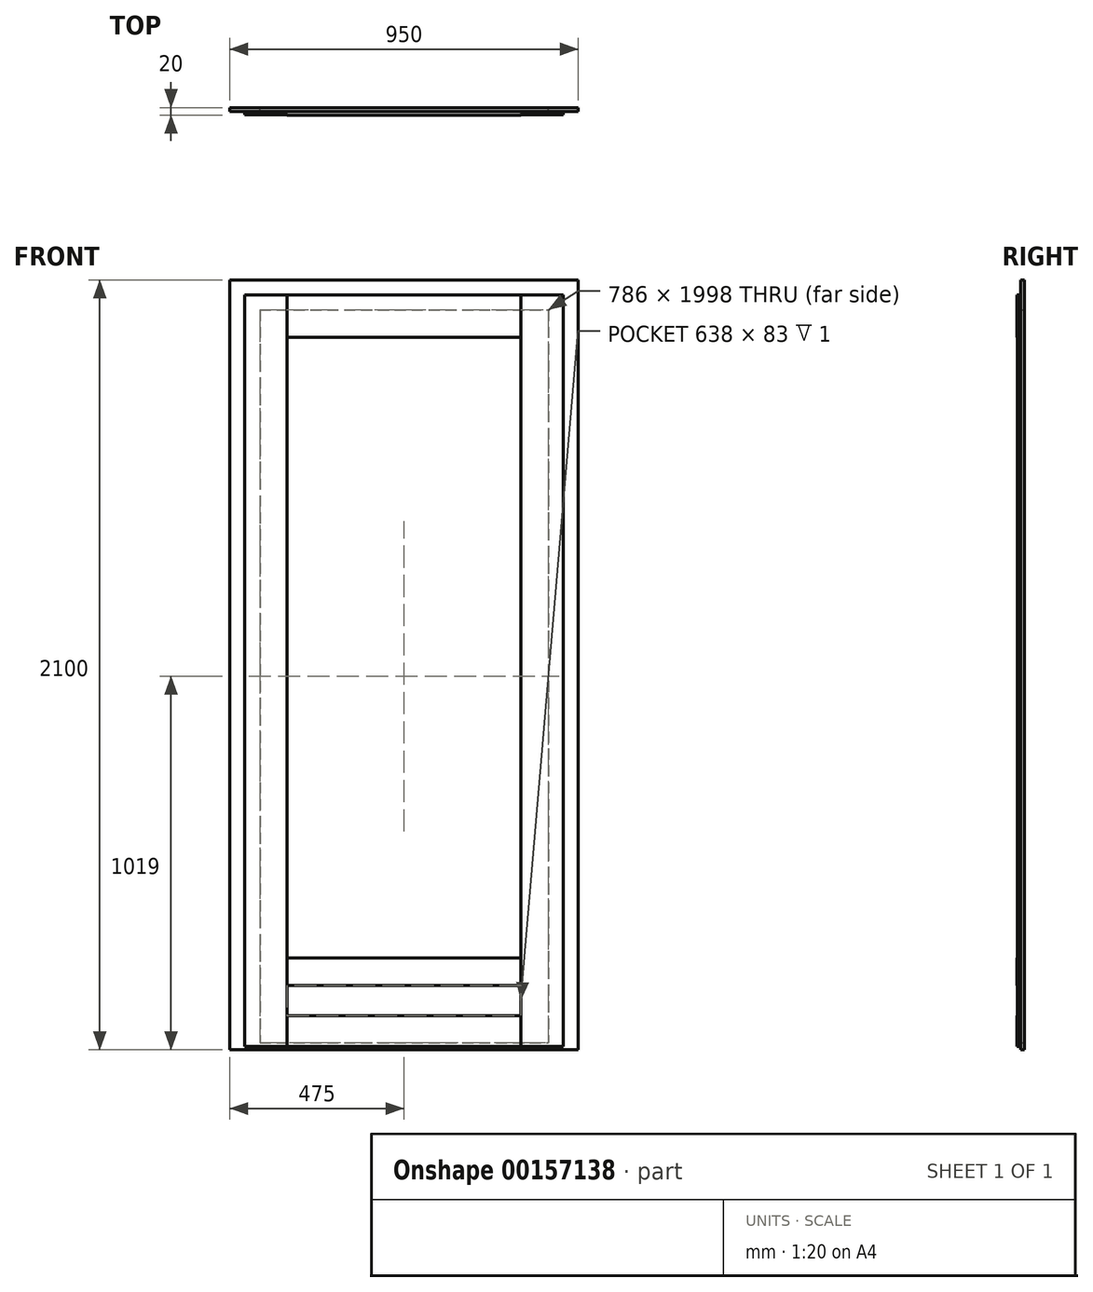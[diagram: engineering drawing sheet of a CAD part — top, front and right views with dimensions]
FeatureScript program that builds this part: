
annotation { "Feature Type Name" : "Feature", "Feature Type Description" : "" }
export const myFeature = defineFeature(function(context is Context, id is Id, definition is map)
    precondition{}
    {
        {
            var Q0;
            Q0=qCreatedBy(makeId("Front.planeOp"),FACE);
            var sketch = newSketch(context, id + "F0", { "sketchPlane" : qUnion([Q0])});
            skLineSegment(sketch, "E0.bottom", {"start": v(0, 0) * mm, "end": v(950, 0) * mm});
            skLineSegment(sketch, "E0.top", {"start": v(0, 2100) * mm, "end": v(950, 2100) * mm});
            skLineSegment(sketch, "E0.left", {"start": v(0, 0) * mm, "end": v(0, 2100) * mm});
            skLineSegment(sketch, "E0.right", {"start": v(950, 0) * mm, "end": v(950, 2100) * mm});
            skLineSegment(sketch, "E1.bottom", {"start": v(82, 2018) * mm, "end": v(868, 2018) * mm});
            skLineSegment(sketch, "E1.top", {"start": v(82, 20) * mm, "end": v(868, 20) * mm});
            skLineSegment(sketch, "E1.left", {"start": v(82, 2018) * mm, "end": v(82, 20) * mm});
            skLineSegment(sketch, "E1.right", {"start": v(868, 2018) * mm, "end": v(868, 20) * mm});
            skSolve(sketch);
        }
        {
            var Q0;
            Q0 = qSketchRegion(id + "F0", true);
            extrude(context, id + "F1", {"entities" : qUnion([Q0]), "depth" : 10 * mm});
        }
        {
            var Q0;
            Q0=makeQuery(id+"F1.opExtrude","CAP_FACE",FACE,{"disambiguationData":[OSD([sQuery(id+"F0.wireOp",EDGE,"E0.bottom"),sQuery(id+"F0.wireOp",EDGE,"E0.top"),sQuery(id+"F0.wireOp",EDGE,"E0.left"),sQuery(id+"F0.wireOp",EDGE,"E0.right"),sQuery(id+"F0.wireOp",EDGE,"E1.bottom"),sQuery(id+"F0.wireOp",EDGE,"E1.top"),sQuery(id+"F0.wireOp",EDGE,"E1.left"),sQuery(id+"F0.wireOp",EDGE,"E1.right")])],"isStart":false});
            var sketch = newSketch(context, id + "F2", { "sketchPlane" : qUnion([Q0])});
            skLineSegment(sketch, "E2.bottom", {"start": v(41, 2059) * mm, "end": v(909, 2059) * mm});
            skLineSegment(sketch, "E2.top", {"start": v(41, 10) * mm, "end": v(909, 10) * mm});
            skLineSegment(sketch, "E2.left", {"start": v(41, 2059) * mm, "end": v(41, 10) * mm});
            skLineSegment(sketch, "E2.right", {"start": v(909, 2059) * mm, "end": v(909, 10) * mm});
            skLineSegment(sketch, "E3.bottom", {"start": v(156, 1944) * mm, "end": v(794, 1944) * mm});
            skLineSegment(sketch, "E3.top", {"start": v(156, 251) * mm, "end": v(794, 251) * mm});
            skLineSegment(sketch, "E3.left", {"start": v(156, 1944) * mm, "end": v(156, 251) * mm});
            skLineSegment(sketch, "E3.right", {"start": v(794, 1944) * mm, "end": v(794, 251) * mm});
            skSolve(sketch);
        }
        {
            var Q0;
            Q0=makeQuery(id+"F2.imprint","IMPRINT",FACE,{"disambiguationData":[TD([[makeQuery(id+"F2.imprint","IMPRINT",EDGE,{"derivedFrom":sQuery(id+"F2.wireOp",EDGE,"E2.bottom")}),-1.0]])]});
            var Q1;
            Q1 = qSketchRegion(id + "F2", true);
            extrude(context, id + "F3", {"entities" : qUnion([Q0, Q1]), "depth" : 10 * mm});
        }
        {
            var Q0;
            Q0=makeQuery(id+"F3.opExtrude","CAP_FACE",FACE,{"disambiguationData":[OSD([sQuery(id+"F2.wireOp",EDGE,"E2.bottom"),sQuery(id+"F2.wireOp",EDGE,"E2.top"),sQuery(id+"F2.wireOp",EDGE,"E2.left"),sQuery(id+"F2.wireOp",EDGE,"E2.right"),sQuery(id+"F2.wireOp",EDGE,"E3.bottom"),sQuery(id+"F2.wireOp",EDGE,"E3.top"),sQuery(id+"F2.wireOp",EDGE,"E3.left"),sQuery(id+"F2.wireOp",EDGE,"E3.right")])],"isStart":false});
            var sketch = newSketch(context, id + "F4", { "sketchPlane" : qUnion([Q0])});
            skLineSegment(sketch, "E4.bottom", {"start": v(41, 2059) * mm, "end": v(156, 2059) * mm});
            skLineSegment(sketch, "E4.top", {"start": v(41, 10) * mm, "end": v(156, 10) * mm});
            skLineSegment(sketch, "E4.left", {"start": v(41, 2059) * mm, "end": v(41, 10) * mm});
            skLineSegment(sketch, "E4.right", {"start": v(156, 2059) * mm, "end": v(156, 10) * mm});
            skLineSegment(sketch, "E5.bottom", {"start": v(794, 2059) * mm, "end": v(909, 2059) * mm});
            skLineSegment(sketch, "E5.top", {"start": v(794, 10) * mm, "end": v(909, 10) * mm});
            skLineSegment(sketch, "E5.left", {"start": v(794, 2059) * mm, "end": v(794, 10) * mm});
            skLineSegment(sketch, "E5.right", {"start": v(909, 2059) * mm, "end": v(909, 10) * mm});
            skSolve(sketch);
        }
        {
            var Q0;
            Q0 = qSketchRegion(id + "F4", true);
            extrude(context, id + "F5", {"entities" : qUnion([Q0]), "operationType" : NewBodyOperationType.REMOVE, "oppositeDirection" : true, "depth" : 1 * mm});
        }
        {
            var Q0;
            {var subQ0=sQuery(id+"F2.wireOp",EDGE,"E2.top");var subQ1=sQuery(id+"F2.wireOp",EDGE,"E3.top");Q0=makeQuery(id+"F5.boolean.opBoolean","SPLIT",FACE,{"disambiguationData":[TD([makeQuery(id+"F3.opExtrude","SWEPT_FACE",FACE,{"disambiguationData":[OSD([subQ0])]})])],"derivedFrom":makeQuery(id+"F3.opExtrude","CAP_FACE",FACE,{"disambiguationData":[OSD([sQuery(id+"F2.wireOp",EDGE,"E2.bottom"),subQ0,sQuery(id+"F2.wireOp",EDGE,"E2.left"),sQuery(id+"F2.wireOp",EDGE,"E2.right"),sQuery(id+"F2.wireOp",EDGE,"E3.bottom"),subQ1,sQuery(id+"F2.wireOp",EDGE,"E3.left"),sQuery(id+"F2.wireOp",EDGE,"E3.right")])],"isStart":false})});}
            var sketch = newSketch(context, id + "F6", { "sketchPlane" : qUnion([Q0])});
            skLineSegment(sketch, "E6.bottom", {"start": v(156, 176) * mm, "end": v(794, 176) * mm});
            skLineSegment(sketch, "E6.top", {"start": v(156, 93) * mm, "end": v(794, 93) * mm});
            skLineSegment(sketch, "E6.left", {"start": v(156, 176) * mm, "end": v(156, 93) * mm});
            skLineSegment(sketch, "E6.right", {"start": v(794, 176) * mm, "end": v(794, 93) * mm});
            skSolve(sketch);
        }
        {
            var Q0;
            Q0=makeQuery(id+"F6.imprint","IMPRINT",FACE,{"disambiguationData":[TD([[makeQuery(id+"F6.imprint","IMPRINT",EDGE,{"derivedFrom":sQuery(id+"F6.wireOp",EDGE,"E6.bottom")}),-1.0]])]});
            extrude(context, id + "F7", {"entities" : qUnion([Q0]), "operationType" : NewBodyOperationType.REMOVE, "oppositeDirection" : true, "depth" : 2 * mm});
        }
    });
